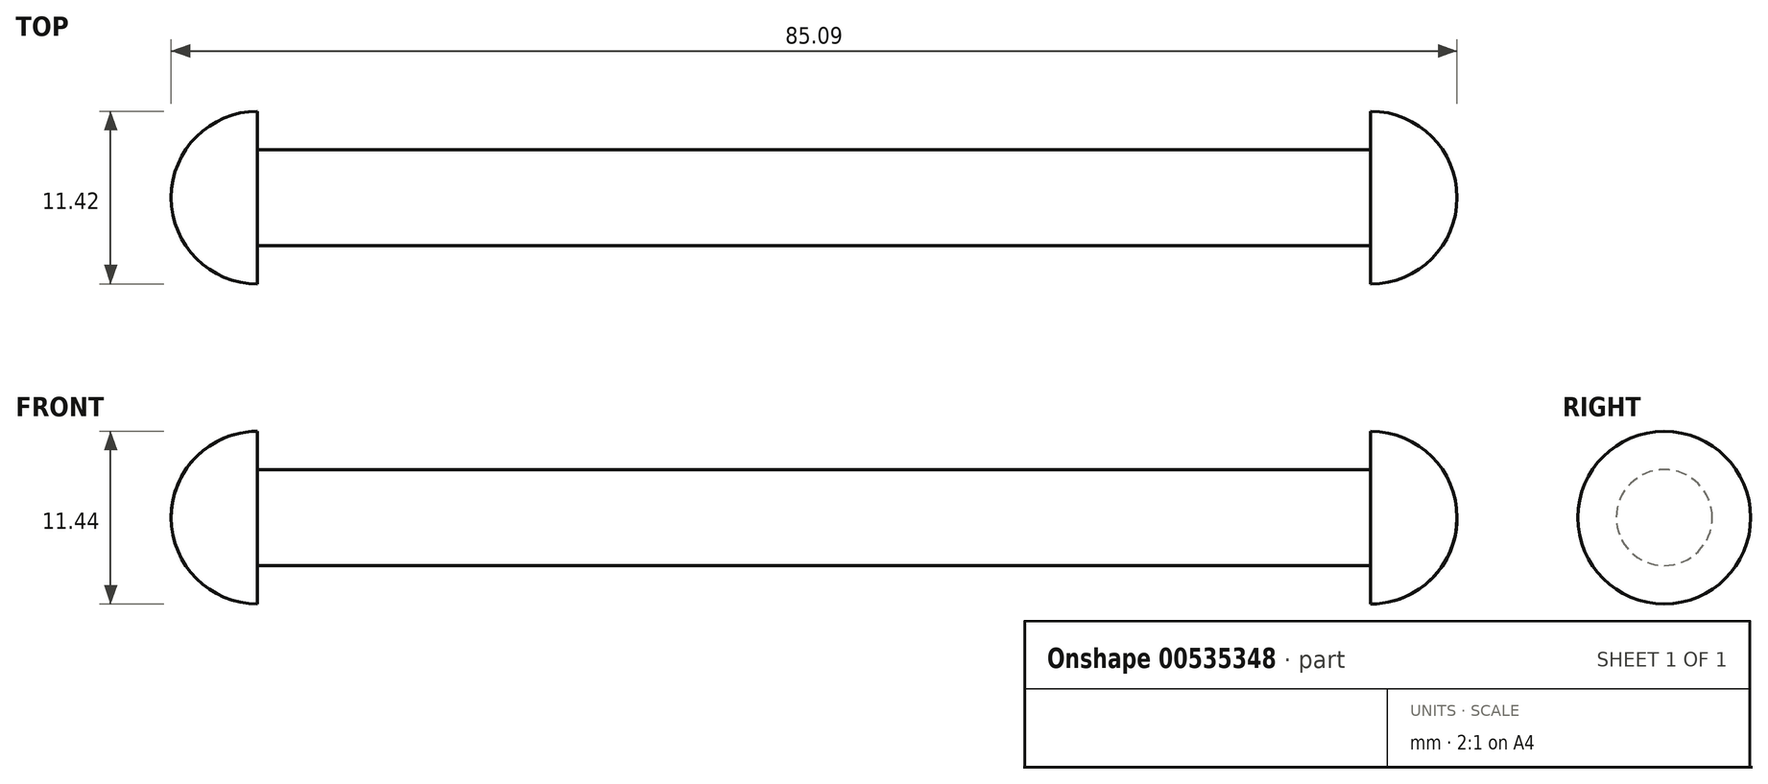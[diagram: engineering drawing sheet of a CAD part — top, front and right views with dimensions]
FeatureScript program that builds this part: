
annotation { "Feature Type Name" : "Feature", "Feature Type Description" : "" }
export const myFeature = defineFeature(function(context is Context, id is Id, definition is map)
    precondition{}
    {
        {
            var Q0;
            Q0=qCreatedBy(makeId("Front.planeOp"),FACE);
            var sketch = newSketch(context, id + "F0", { "sketchPlane" : qUnion([Q0])});
            skLineSegment(sketch, "E0", {"start": v(-79.38, 5.71) * mm, "end": v(-79.38, 3.17) * mm});
            skLineSegment(sketch, "E1", {"start": v(-79.38, 3.17) * mm, "end": v(-5.71, 3.17) * mm});
            skLineSegment(sketch, "E2", {"start": v(-5.72, 3.17) * mm, "end": v(-5.72, 5.72) * mm});
            skLineSegment(sketch, "E3", {"start": v(0, 0) * mm, "end": v(-85.1, 0) * mm});
            skArc(sketch, "E4", {"start": v(0, 0) * mm, "mid": v(-1.67, 4.04) * mm, "end": v(-5.72, 5.72) * mm});
            skArc(sketch, "E5", {"start": v(-79.38, 5.71) * mm, "mid": v(-83.42, 4.04) * mm, "end": v(-85.1, 0) * mm});
            skLineSegment(sketch, "E6", {"start": v(0, 0) * mm, "end": v(16.7, 0) * mm, "construction": true});
            skPoint(sketch, "E7", {"position": v(-42.55, 3.17) * mm});
            skSolve(sketch);
        }
        {
            var Q0;
            Q0=makeQuery(id+"F0.imprint","IMPRINT",FACE,{"disambiguationData":[TD([[makeQuery(id+"F0.imprint","IMPRINT",EDGE,{"derivedFrom":sQuery(id+"F0.wireOp",EDGE,"E0")}),-1.0]])]});
            var Q1;
            Q1=sQuery(id+"F0.wireOp",EDGE,"E6");
            revolve(context, id + "F1", {"entities" : qUnion([Q0]), "axis" : qUnion([Q1]), "revolveType" : RevolveType.FULL});
        }
    });
